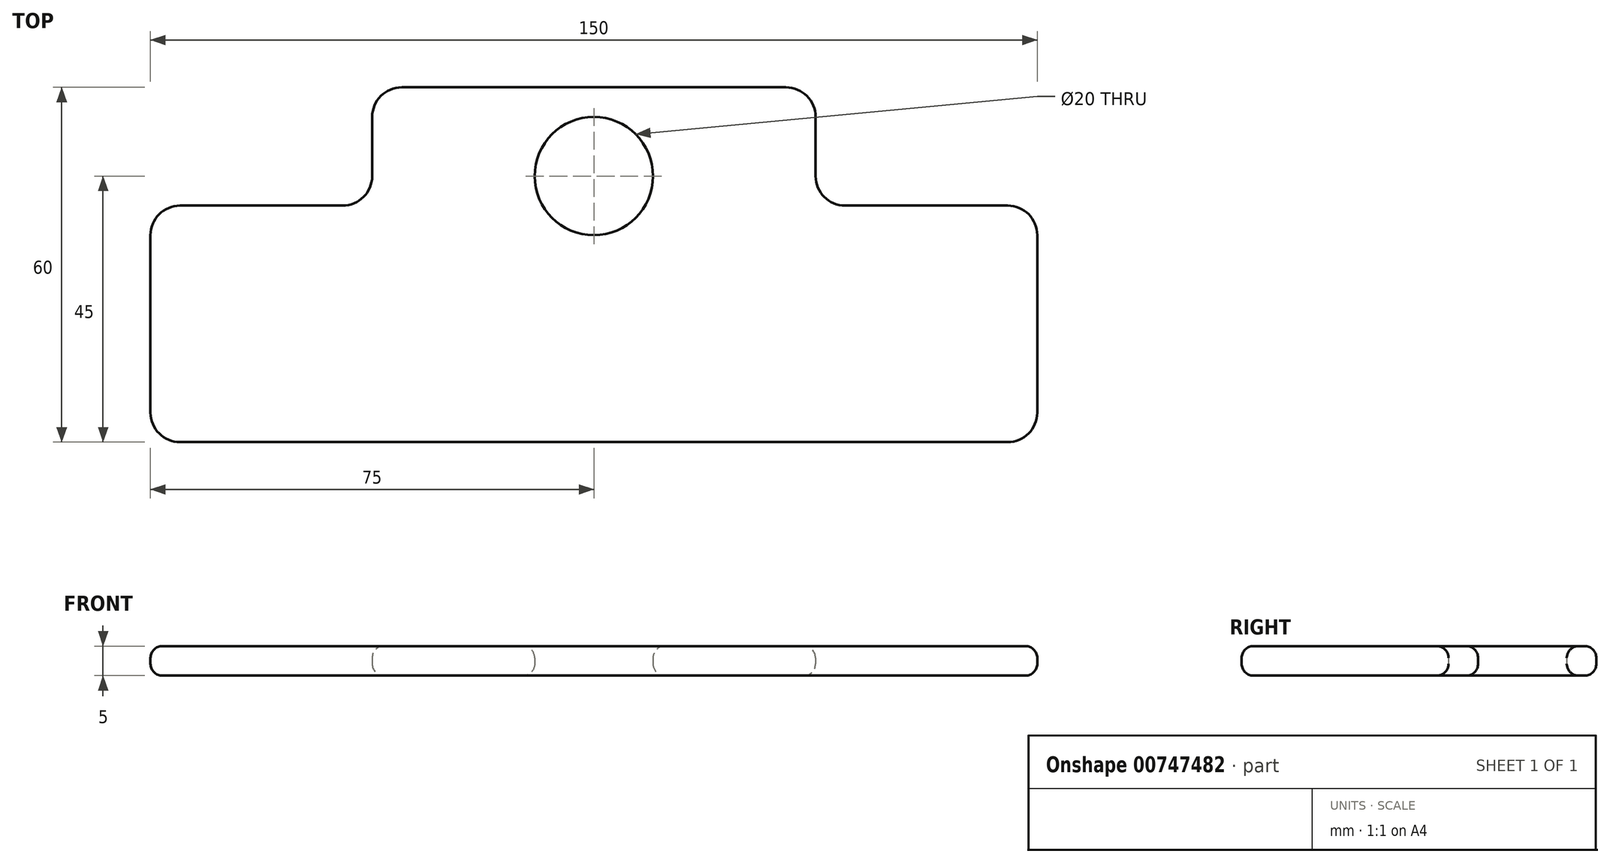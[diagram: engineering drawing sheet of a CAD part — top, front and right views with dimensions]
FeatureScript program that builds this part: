
annotation { "Feature Type Name" : "Feature", "Feature Type Description" : "" }
export const myFeature = defineFeature(function(context is Context, id is Id, definition is map)
    precondition{}
    {
        {
            var Q0;
            Q0=qCreatedBy(makeId("Top.planeOp"),FACE);
            var sketch = newSketch(context, id + "F0", { "sketchPlane" : qUnion([Q0])});
            skLineSegment(sketch, "E0.bottom", {"start": v(-70, 40) * mm, "end": v(-42.5, 40) * mm});
            skLineSegment(sketch, "E0.top", {"start": v(-70, 0) * mm, "end": v(70, 0) * mm});
            skLineSegment(sketch, "E0.left", {"start": v(-75, 35) * mm, "end": v(-75, 5) * mm});
            skLineSegment(sketch, "E0.right", {"start": v(75, 35) * mm, "end": v(75, 5) * mm});
            skPoint(sketch, "E1.visualSharp", {"position": v(-75, 0) * mm});
            skArc(sketch, "E1.filletArc", {"start": v(-75, 5) * mm, "mid": v(-73.54, 1.46) * mm, "end": v(-70, 0) * mm});
            skPoint(sketch, "E2.visualSharp", {"position": v(75, 0) * mm});
            skArc(sketch, "E2.filletArc", {"start": v(70, 0) * mm, "mid": v(73.54, 1.46) * mm, "end": v(75, 5) * mm});
            skLineSegment(sketch, "E3.bottom", {"start": v(-32.5, 60) * mm, "end": v(32.5, 60) * mm});
            skLineSegment(sketch, "E3.left", {"start": v(-37.5, 55) * mm, "end": v(-37.5, 45) * mm});
            skLineSegment(sketch, "E3.right", {"start": v(37.5, 55) * mm, "end": v(37.5, 45) * mm});
            skLineSegment(sketch, "E4.trimOffspring", {"start": v(42.5, 40) * mm, "end": v(70, 40) * mm});
            skPoint(sketch, "E5.visualSharp", {"position": v(-37.5, 40) * mm});
            skArc(sketch, "E5.filletArc", {"start": v(-42.5, 40) * mm, "mid": v(-38.96, 41.46) * mm, "end": v(-37.5, 45) * mm});
            skPoint(sketch, "E6.visualSharp", {"position": v(37.5, 40) * mm});
            skArc(sketch, "E6.filletArc", {"start": v(37.5, 45) * mm, "mid": v(38.96, 41.46) * mm, "end": v(42.5, 40) * mm});
            skPoint(sketch, "E7.visualSharp", {"position": v(37.5, 60) * mm});
            skArc(sketch, "E7.filletArc", {"start": v(37.5, 55) * mm, "mid": v(36.04, 58.54) * mm, "end": v(32.5, 60) * mm});
            skPoint(sketch, "E8.visualSharp", {"position": v(-37.5, 60) * mm});
            skArc(sketch, "E8.filletArc", {"start": v(-32.5, 60) * mm, "mid": v(-36.04, 58.54) * mm, "end": v(-37.5, 55) * mm});
            skPoint(sketch, "E9.visualSharp", {"position": v(75, 40) * mm});
            skArc(sketch, "E9.filletArc", {"start": v(75, 35) * mm, "mid": v(73.54, 38.54) * mm, "end": v(70, 40) * mm});
            skPoint(sketch, "E10.visualSharp", {"position": v(-75, 40) * mm});
            skArc(sketch, "E10.filletArc", {"start": v(-70, 40) * mm, "mid": v(-73.54, 38.54) * mm, "end": v(-75, 35) * mm});
            skCircle(sketch, "E11", {"center": v(0, 45) * mm, "radius": 10 * mm});
            skSolve(sketch);
        }
        {
            var Q0;
            Q0=makeQuery(id+"F0.imprint","IMPRINT",FACE,{"disambiguationData":[TD([[makeQuery(id+"F0.imprint","IMPRINT",EDGE,{"derivedFrom":sQuery(id+"F0.wireOp",EDGE,"E0.bottom")}),-1.0]])]});
            extrude(context, id + "F1", {"entities" : qUnion([Q0]), "depth" : 5 * mm, "offsetDistance" : 25 * mm});
        }
        {
            var Q0;
            Q0=makeQuery(id+"F1.opExtrude","CAP_EDGE",EDGE,{"disambiguationData":[OSD([sQuery(id+"F0.wireOp",EDGE,"E0.top")])],"isStart":false});
            var Q1;
            Q1=makeQuery(id+"F1.opExtrude","CAP_EDGE",EDGE,{"disambiguationData":[OSD([sQuery(id+"F0.wireOp",EDGE,"E0.top")])],"isStart":true});
            var Q2;
            Q2=makeQuery(id+"F1.opExtrude","CAP_EDGE",EDGE,{"disambiguationData":[OSD([sQuery(id+"F0.wireOp",EDGE,"E11")])],"isStart":false});
            var Q3;
            Q3=makeQuery(id+"F1.opExtrude","CAP_EDGE",EDGE,{"disambiguationData":[OSD([sQuery(id+"F0.wireOp",EDGE,"E11")])],"isStart":true});
            fillet(context, id + "F2", {"entities" : qUnion([Q0, Q1, Q2, Q3]), "radius" : 2 * mm, "tangentPropagation" : true, "allowEdgeOverflow" : false});
        }
    });
